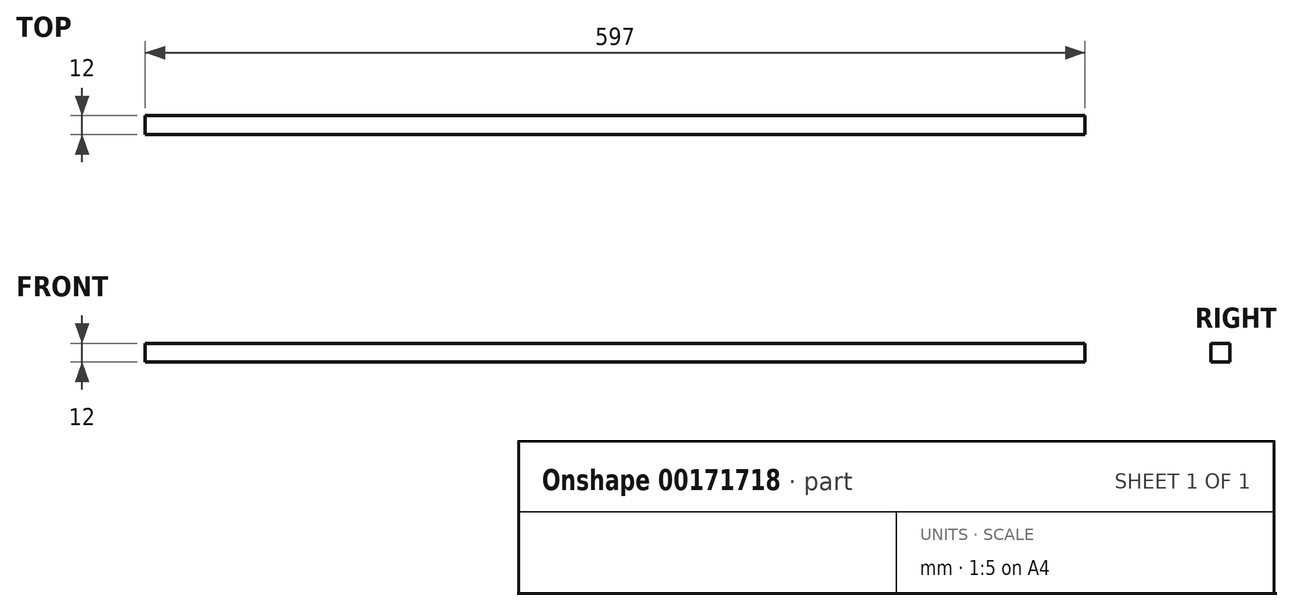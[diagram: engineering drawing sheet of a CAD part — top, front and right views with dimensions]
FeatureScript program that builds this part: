
annotation { "Feature Type Name" : "Feature", "Feature Type Description" : "" }
export const myFeature = defineFeature(function(context is Context, id is Id, definition is map)
    precondition{}
    {
        {
            var Q0;
            Q0=qCreatedBy(makeId("Right.planeOp"),FACE);
            var sketch = newSketch(context, id + "F0", { "sketchPlane" : qUnion([Q0])});
            skLineSegment(sketch, "E0.bottom", {"start": v(-6, 6) * mm, "end": v(6, 6) * mm});
            skLineSegment(sketch, "E0.top", {"start": v(-6, -6) * mm, "end": v(6, -6) * mm});
            skLineSegment(sketch, "E0.left", {"start": v(-6, 6) * mm, "end": v(-6, -6) * mm});
            skLineSegment(sketch, "E0.right", {"start": v(6, 6) * mm, "end": v(6, -6) * mm});
            skPoint(sketch, "E0.middle", {"position": v(0, 0) * mm});
            skSolve(sketch);
        }
        {
            var Q0;
            Q0=makeQuery(id+"F0.imprint","IMPRINT",FACE,{"disambiguationData":[TD([[makeQuery(id+"F0.imprint","IMPRINT",EDGE,{"derivedFrom":sQuery(id+"F0.wireOp",EDGE,"E0.bottom")}),-1.0]])]});
            extrude(context, id + "F1", {"entities" : qUnion([Q0]), "depth" : 597 * mm});
        }
    });
